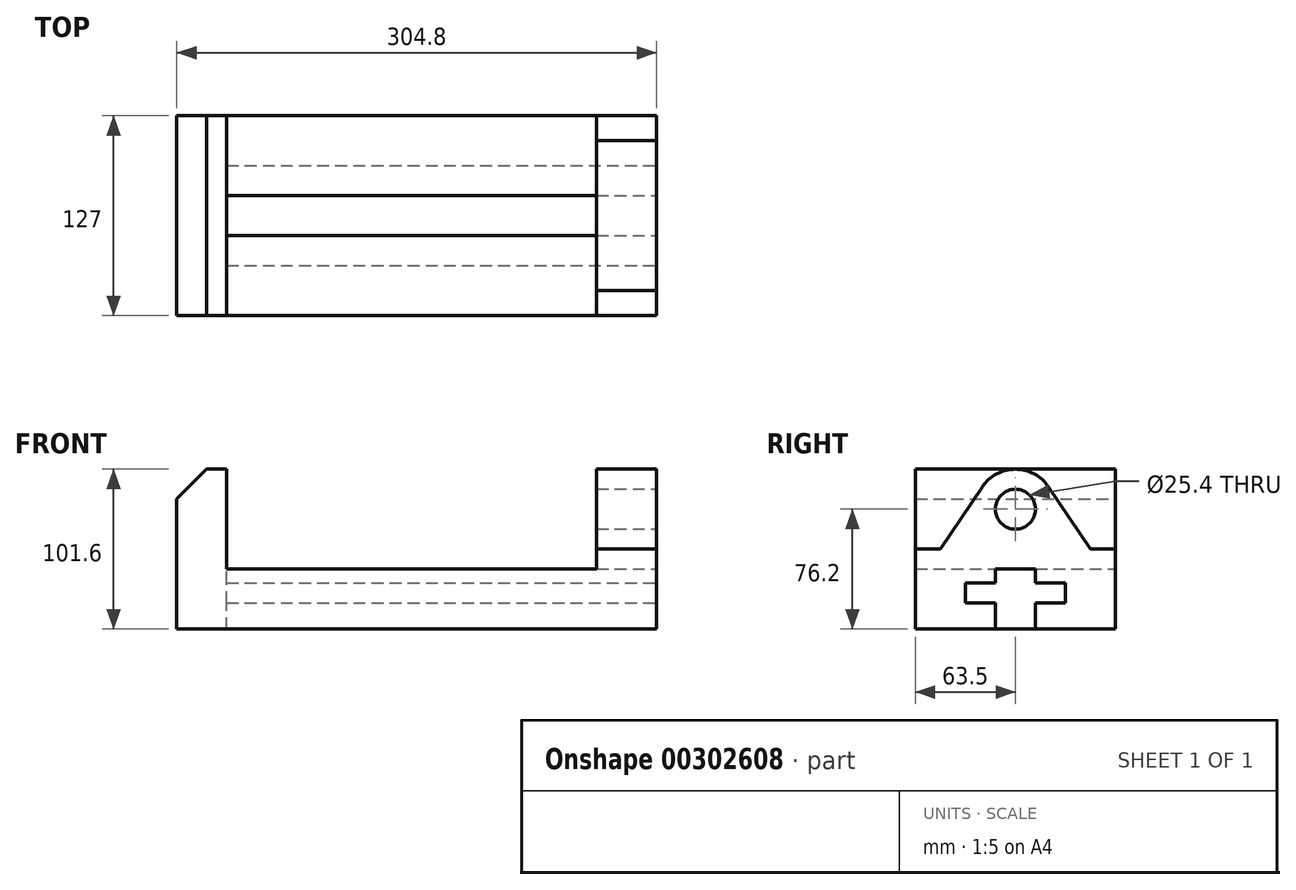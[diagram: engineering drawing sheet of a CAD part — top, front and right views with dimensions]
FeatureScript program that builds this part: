
annotation { "Feature Type Name" : "Feature", "Feature Type Description" : "" }
export const myFeature = defineFeature(function(context is Context, id is Id, definition is map)
    precondition{}
    {
        {
            var Q0;
            Q0=qCreatedBy(makeId("Front.planeOp"),FACE);
            var sketch = newSketch(context, id + "F0", { "sketchPlane" : qUnion([Q0])});
            skLineSegment(sketch, "E0", {"start": v(0, 0) * mm, "end": v(0, 101.6) * mm});
            skLineSegment(sketch, "E1", {"start": v(0, 101.6) * mm, "end": v(31.75, 101.6) * mm});
            skLineSegment(sketch, "E2", {"start": v(31.75, 101.6) * mm, "end": v(31.75, 38.1) * mm});
            skLineSegment(sketch, "E3", {"start": v(31.75, 38.1) * mm, "end": v(266.7, 38.1) * mm});
            skLineSegment(sketch, "E4", {"start": v(266.7, 38.1) * mm, "end": v(266.7, 50.8) * mm});
            skLineSegment(sketch, "E5", {"start": v(266.7, 50.8) * mm, "end": v(304.8, 50.8) * mm});
            skLineSegment(sketch, "E6", {"start": v(304.8, 50.8) * mm, "end": v(304.8, 0) * mm});
            skLineSegment(sketch, "E7", {"start": v(304.8, 0) * mm, "end": v(0, 0) * mm});
            skSolve(sketch);
        }
        {
            var Q0;
            Q0 = qSketchRegion(id + "F0", true);
            extrude(context, id + "F1", {"entities" : qUnion([Q0]), "endBound" : BoundingType.SYMMETRIC, "depth" : 127 * mm});
        }
        {
            var Q0;
            Q0=makeQuery(id+"F1.opExtrude","SWEPT_EDGE",EDGE,{"disambiguationData":[OSD([sQuery(id+"F0.wireOp",EDGE,"E0"),sQuery(id+"F0.wireOp",EDGE,"E1")])]});
            chamfer(context, id + "F2", {"entities" : qUnion([Q0]), "chamferType" : ChamferType.TWO_OFFSETS, "width1" : 19.05 * mm, "oppositeDirection" : false, "width2" : 19.05 * mm, "tangentPropagation" : true});
        }
        {
            var Q0;
            {var subQ0=sQuery(id+"F0.wireOp",EDGE,"E6");Q0=makeQuery(id+"F6.boolean.opBoolean","MERGE",FACE,{"derivedFrom":[makeQuery(id+"F1.opExtrude","SWEPT_FACE",FACE,{"disambiguationData":[OSD([subQ0])]}),makeQuery(id+"F6.opExtrude","CAP_FACE",FACE,{"disambiguationData":[OSD([sQuery(id+"F0.wireOp",EDGE,"E5"),subQ0,sQuery(id+"F5.wireOp",EDGE,"E20"),sQuery(id+"F5.wireOp",EDGE,"E21"),sQuery(id+"F5.wireOp",EDGE,"E22"),sQuery(id+"F5.wireOp",EDGE,"E23")])],"isStart":true})]});}
            var sketch = newSketch(context, id + "F3", { "sketchPlane" : qUnion([Q0])});
            skLineSegment(sketch, "E8", {"start": v(-12.7, 0) * mm, "end": v(12.7, 0) * mm});
            skLineSegment(sketch, "E9", {"start": v(12.7, 0) * mm, "end": v(12.7, 16.51) * mm});
            skLineSegment(sketch, "E10", {"start": v(12.7, 16.51) * mm, "end": v(31.75, 16.51) * mm});
            skLineSegment(sketch, "E11", {"start": v(31.75, 16.51) * mm, "end": v(31.75, 29.21) * mm});
            skLineSegment(sketch, "E12", {"start": v(31.75, 29.21) * mm, "end": v(12.7, 29.21) * mm});
            skLineSegment(sketch, "E13", {"start": v(12.7, 29.21) * mm, "end": v(12.7, 38.1) * mm});
            skLineSegment(sketch, "E14", {"start": v(12.7, 38.1) * mm, "end": v(-12.7, 38.1) * mm});
            skLineSegment(sketch, "E15", {"start": v(-12.7, 38.1) * mm, "end": v(-12.7, 29.21) * mm});
            skLineSegment(sketch, "E16", {"start": v(-12.7, 29.21) * mm, "end": v(-31.75, 29.21) * mm});
            skLineSegment(sketch, "E17", {"start": v(-31.75, 29.21) * mm, "end": v(-31.75, 16.51) * mm});
            skLineSegment(sketch, "E18", {"start": v(-31.75, 16.51) * mm, "end": v(-12.7, 16.51) * mm});
            skLineSegment(sketch, "E19", {"start": v(-12.7, 16.51) * mm, "end": v(-12.7, 0) * mm});
            skSolve(sketch);
        }
        {
            var Q0;
            Q0 = qSketchRegion(id + "F3", true);
            var Q1;
            Q1=makeQuery(id+"F1.opExtrude","SWEPT_FACE",FACE,{"disambiguationData":[OSD([sQuery(id+"F0.wireOp",EDGE,"E2")])]});
            extrude(context, id + "F4", {"entities" : qUnion([Q0]), "operationType" : NewBodyOperationType.REMOVE, "endBound" : BoundingType.UP_TO_SURFACE, "oppositeDirection" : true, "endBoundEntityFace" : qUnion([Q1]), "depth" : 25.4 * mm});
        }
        {
            var Q0;
            Q0=makeQuery(id+"F1.opExtrude","SWEPT_FACE",FACE,{"disambiguationData":[OSD([sQuery(id+"F0.wireOp",EDGE,"E6")])]});
            var sketch = newSketch(context, id + "F5", { "sketchPlane" : qUnion([Q0])});
            skCircle(sketch, "E20", {"center": v(0, 76.2) * mm, "radius": 12.7 * mm});
            skLineSegment(sketch, "E21", {"start": v(-47.63, 50.8) * mm, "end": v(-21.1, 90.35) * mm});
            skArc(sketch, "E22", {"start": v(21.1, 90.35) * mm, "mid": v(0, 101.6) * mm, "end": v(-21.1, 90.35) * mm});
            skLineSegment(sketch, "E23", {"start": v(21.1, 90.35) * mm, "end": v(47.63, 50.8) * mm});
            skSolve(sketch);
        }
        {
            var Q0;
            Q0=makeQuery(id+"F5.imprint","IMPRINT",FACE,{"disambiguationData":[TD([[makeQuery(id+"F5.imprint","IMPRINT",EDGE,{"derivedFrom":sQuery(id+"F5.wireOp",EDGE,"E20")}),-1.0]])]});
            extrude(context, id + "F6", {"entities" : qUnion([Q0]), "operationType" : NewBodyOperationType.ADD, "oppositeDirection" : true, "depth" : 38.1 * mm});
        }
    });
